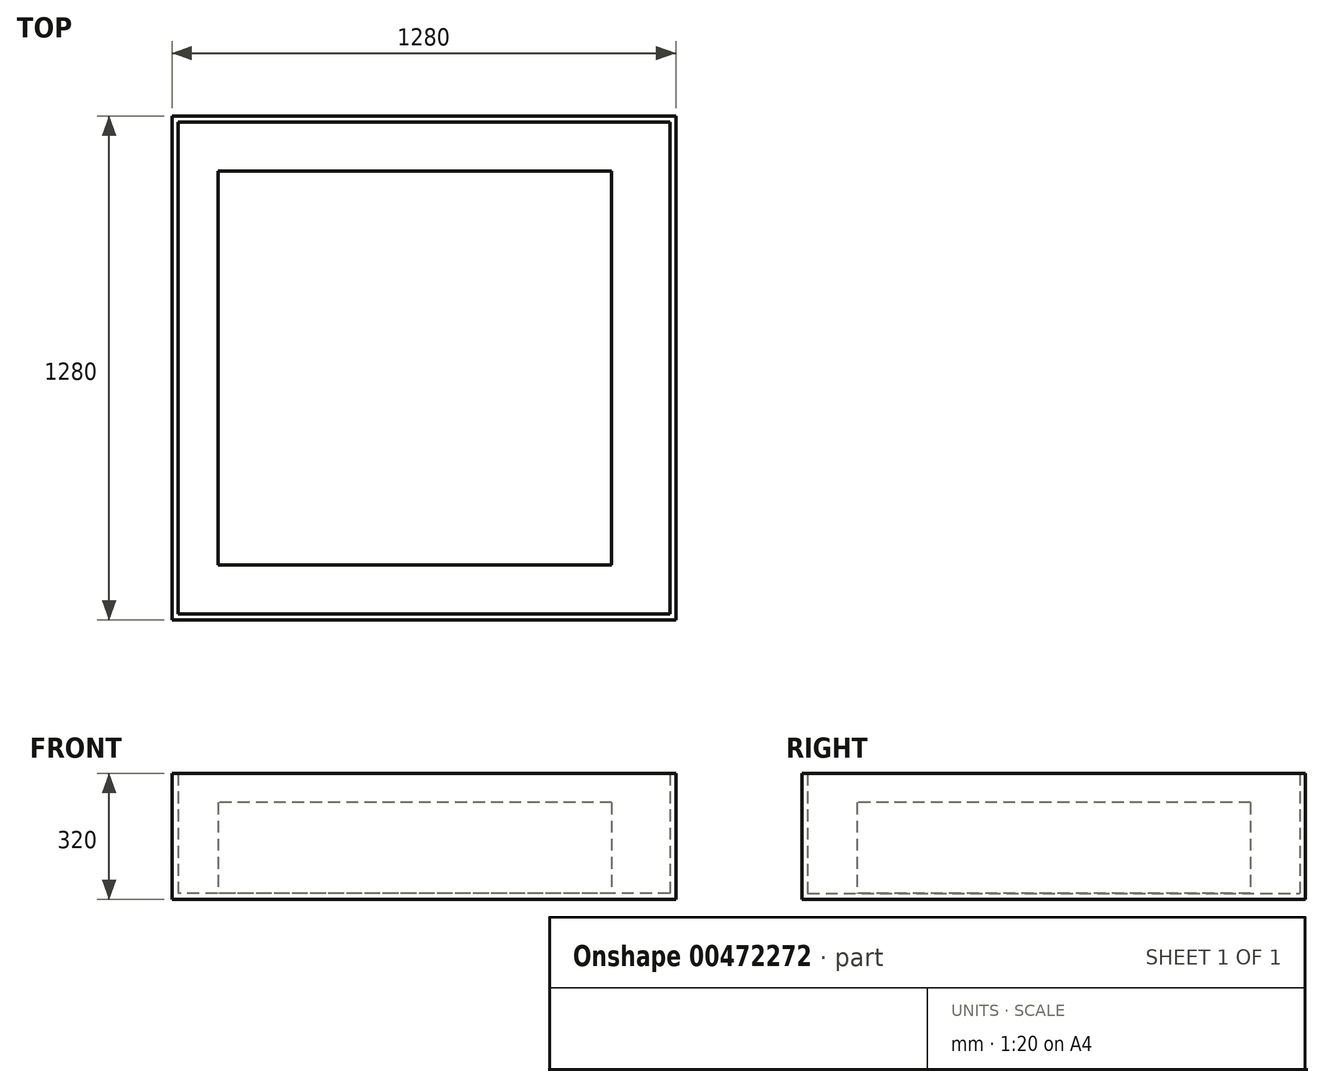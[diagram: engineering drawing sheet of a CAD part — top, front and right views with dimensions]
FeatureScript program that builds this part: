
annotation { "Feature Type Name" : "Feature", "Feature Type Description" : "" }
export const myFeature = defineFeature(function(context is Context, id is Id, definition is map)
    precondition{}
    {
        {
            var Q0;
            Q0=qCreatedBy(makeId("Top.planeOp"),FACE);
            var sketch = newSketch(context, id + "F0", { "sketchPlane" : qUnion([Q0])});
            skLineSegment(sketch, "E0.bottom", {"start": v(625, -625) * mm, "end": v(-625, -625) * mm});
            skLineSegment(sketch, "E0.top", {"start": v(625, 625) * mm, "end": v(-625, 625) * mm});
            skLineSegment(sketch, "E0.left", {"start": v(625, -625) * mm, "end": v(625, 625) * mm});
            skLineSegment(sketch, "E0.right", {"start": v(-625, -625) * mm, "end": v(-625, 625) * mm});
            skPoint(sketch, "E0.middle", {"position": v(0, 0) * mm});
            skSolve(sketch);
        }
        {
            var Q0;
            Q0 = qSketchRegion(id + "F0", true);
            extrude(context, id + "F1", {"entities" : qUnion([Q0]), "depth" : 15 * mm});
        }
        {
            var Q0;
            Q0=makeQuery(id+"F1.opExtrude","SWEPT_FACE",FACE,{"disambiguationData":[OSD([sQuery(id+"F0.wireOp",EDGE,"E0.bottom")])]});
            var sketch = newSketch(context, id + "F2", { "sketchPlane" : qUnion([Q0])});
            skLineSegment(sketch, "E1.bottom", {"start": v(-625, 0) * mm, "end": v(640, 0) * mm});
            skLineSegment(sketch, "E1.top", {"start": v(-625, 320) * mm, "end": v(640, 320) * mm});
            skLineSegment(sketch, "E1.left", {"start": v(-625, 0) * mm, "end": v(-625, 320) * mm});
            skLineSegment(sketch, "E1.right", {"start": v(640, 0) * mm, "end": v(640, 320) * mm});
            skSolve(sketch);
        }
        {
            var Q0;
            Q0=makeQuery(id+"F1.opExtrude","SWEPT_FACE",FACE,{"disambiguationData":[OSD([sQuery(id+"F0.wireOp",EDGE,"E0.left")])]});
            var sketch = newSketch(context, id + "F3", { "sketchPlane" : qUnion([Q0])});
            skLineSegment(sketch, "E2.bottom", {"start": v(-625, 0) * mm, "end": v(640, 0) * mm});
            skLineSegment(sketch, "E2.top", {"start": v(-625, 320) * mm, "end": v(640, 320) * mm});
            skLineSegment(sketch, "E2.left", {"start": v(-625, 0) * mm, "end": v(-625, 320) * mm});
            skLineSegment(sketch, "E2.right", {"start": v(640, 0) * mm, "end": v(640, 320) * mm});
            skSolve(sketch);
        }
        {
            var Q0;
            Q0=makeQuery(id+"F1.opExtrude","SWEPT_FACE",FACE,{"disambiguationData":[OSD([sQuery(id+"F0.wireOp",EDGE,"E0.top")])]});
            var sketch = newSketch(context, id + "F4", { "sketchPlane" : qUnion([Q0])});
            skLineSegment(sketch, "E3.bottom", {"start": v(-625, 0) * mm, "end": v(640, 0) * mm});
            skLineSegment(sketch, "E3.top", {"start": v(-625, 320) * mm, "end": v(640, 320) * mm});
            skLineSegment(sketch, "E3.left", {"start": v(-625, 0) * mm, "end": v(-625, 320) * mm});
            skLineSegment(sketch, "E3.right", {"start": v(640, 0) * mm, "end": v(640, 320) * mm});
            skSolve(sketch);
        }
        {
            var Q0;
            Q0=makeQuery(id+"F1.opExtrude","SWEPT_FACE",FACE,{"disambiguationData":[OSD([sQuery(id+"F0.wireOp",EDGE,"E0.right")])]});
            var sketch = newSketch(context, id + "F5", { "sketchPlane" : qUnion([Q0])});
            skLineSegment(sketch, "E4.bottom", {"start": v(-625, 0) * mm, "end": v(640, 0) * mm});
            skLineSegment(sketch, "E4.top", {"start": v(-625, 320) * mm, "end": v(640, 320) * mm});
            skLineSegment(sketch, "E4.left", {"start": v(-625, 0) * mm, "end": v(-625, 320) * mm});
            skLineSegment(sketch, "E4.right", {"start": v(640, 0) * mm, "end": v(640, 320) * mm});
            skSolve(sketch);
        }
        {
            var Q0;
            Q0 = qSketchRegion(id + "F2", true);
            extrude(context, id + "F6", {"entities" : qUnion([Q0]), "operationType" : NewBodyOperationType.ADD, "depth" : 15 * mm});
        }
        {
            var Q0;
            Q0 = qSketchRegion(id + "F3", true);
            extrude(context, id + "F7", {"entities" : qUnion([Q0]), "operationType" : NewBodyOperationType.ADD, "depth" : 15 * mm});
        }
        {
            var Q0;
            Q0 = qSketchRegion(id + "F4", true);
            extrude(context, id + "F8", {"entities" : qUnion([Q0]), "operationType" : NewBodyOperationType.ADD, "depth" : 15 * mm});
        }
        {
            var Q0;
            Q0 = qSketchRegion(id + "F5", true);
            extrude(context, id + "F9", {"entities" : qUnion([Q0]), "operationType" : NewBodyOperationType.ADD, "depth" : 15 * mm});
        }
        {
            var Q0;
            Q0=qCreatedBy(makeId("Top.planeOp"),FACE);
            cPlane(context, id + "F10", {"entities" : qUnion([Q0]), "cplaneType" : CPlaneType.OFFSET, "offset" : 320 * mm, "width" : 150 * mm, "height" : 150 * mm});
        }
        {
            var Q0;
            Q0=makeQuery(id+"F1.opExtrude","CAP_FACE",FACE,{"disambiguationData":[OSD([sQuery(id+"F0.wireOp",EDGE,"E0.bottom"),sQuery(id+"F0.wireOp",EDGE,"E0.top"),sQuery(id+"F0.wireOp",EDGE,"E0.left"),sQuery(id+"F0.wireOp",EDGE,"E0.right")])],"isStart":false});
            var sketch = newSketch(context, id + "F11", { "sketchPlane" : qUnion([Q0])});
            skLineSegment(sketch, "E5.bottom", {"start": v(477.13, 500) * mm, "end": v(-522.87, 500) * mm});
            skLineSegment(sketch, "E5.top", {"start": v(477.13, -500) * mm, "end": v(-522.87, -500) * mm});
            skLineSegment(sketch, "E5.left", {"start": v(477.13, 500) * mm, "end": v(477.13, -500) * mm});
            skLineSegment(sketch, "E5.right", {"start": v(-522.87, 500) * mm, "end": v(-522.87, -500) * mm});
            skPoint(sketch, "E5.middle", {"position": v(-22.87, 0) * mm});
            skSolve(sketch);
        }
        {
            var Q0;
            Q0 = qSketchRegion(id + "F11", true);
            extrude(context, id + "F12", {"entities" : qUnion([Q0]), "operationType" : NewBodyOperationType.ADD, "depth" : 231 * mm});
        }
    });
